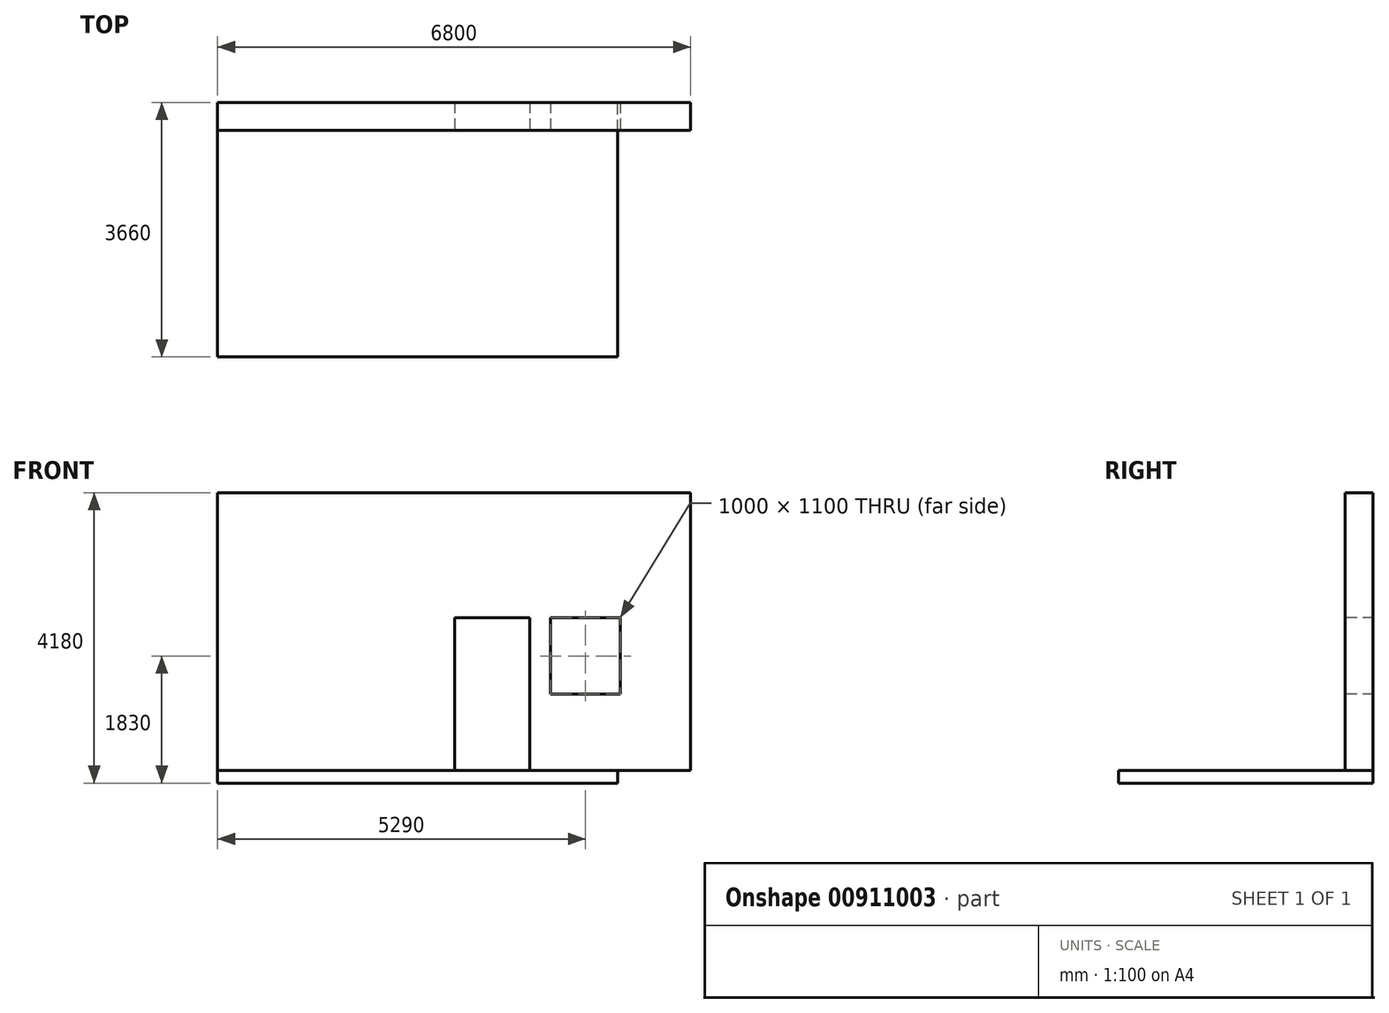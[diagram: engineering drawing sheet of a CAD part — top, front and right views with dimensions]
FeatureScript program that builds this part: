
annotation { "Feature Type Name" : "Feature", "Feature Type Description" : "" }
export const myFeature = defineFeature(function(context is Context, id is Id, definition is map)
    precondition{}
    {
        {
            var Q0;
            Q0=qCreatedBy(makeId("Top.planeOp"),FACE);
            var sketch = newSketch(context, id + "F0", { "sketchPlane" : qUnion([Q0])});
            skLineSegment(sketch, "E0.bottom", {"start": v(0, 0) * mm, "end": v(5750, 0) * mm});
            skLineSegment(sketch, "E0.top", {"start": v(0, 3500) * mm, "end": v(5750, 3500) * mm});
            skLineSegment(sketch, "E0.left", {"start": v(0, 0) * mm, "end": v(0, 3500) * mm});
            skLineSegment(sketch, "E0.right", {"start": v(5750, 0) * mm, "end": v(5750, 3500) * mm});
            skSolve(sketch);
        }
        {
            var Q0;
            Q0=makeQuery(id+"F0.imprint","IMPRINT",FACE,{"disambiguationData":[TD([[makeQuery(id+"F0.imprint","IMPRINT",EDGE,{"derivedFrom":sQuery(id+"F0.wireOp",EDGE,"E0.bottom")}),1.0]])]});
            extrude(context, id + "F1", {"entities" : qUnion([Q0]), "depth" : 180 * mm, "offsetDistance" : 25 * mm});
        }
        {
            var Q0;
            Q0=makeQuery(id+"F1.opExtrude","SWEPT_FACE",FACE,{"disambiguationData":[OSD([sQuery(id+"F0.wireOp",EDGE,"E0.top")])]});
            var sketch = newSketch(context, id + "F2", { "sketchPlane" : qUnion([Q0])});
            skLineSegment(sketch, "E1.bottom", {"start": v(-5750, 180) * mm, "end": v(0, 180) * mm});
            skLineSegment(sketch, "E1.top", {"start": v(-5750, 0) * mm, "end": v(0, 0) * mm});
            skLineSegment(sketch, "E1.left", {"start": v(-5750, 180) * mm, "end": v(-5750, 0) * mm});
            skLineSegment(sketch, "E1.right", {"start": v(0, 180) * mm, "end": v(0, 0) * mm});
            skSolve(sketch);
        }
        {
            var Q0;
            Q0=makeQuery(id+"F2.imprint","IMPRINT",FACE,{"disambiguationData":[TD([[makeQuery(id+"F2.imprint","IMPRINT",EDGE,{"derivedFrom":sQuery(id+"F2.wireOp",EDGE,"E1.bottom")}),1.0]])]});
            extrude(context, id + "F3", {"entities" : qUnion([Q0]), "operationType" : NewBodyOperationType.ADD, "depth" : 160 * mm, "offsetDistance" : 25 * mm});
        }
        {
            var Q0;
            Q0=makeQuery(id+"F3.boolean.opBoolean","MERGE",FACE,{"derivedFrom":[makeQuery(id+"F1.opExtrude","CAP_FACE",FACE,{"disambiguationData":[OSD([sQuery(id+"F0.wireOp",EDGE,"E0.bottom"),sQuery(id+"F0.wireOp",EDGE,"E0.top"),sQuery(id+"F0.wireOp",EDGE,"E0.left"),sQuery(id+"F0.wireOp",EDGE,"E0.right")])],"isStart":false}),makeQuery(id+"F3.opExtrude","SWEPT_FACE",FACE,{"disambiguationData":[OSD([sQuery(id+"F2.wireOp",EDGE,"E1.bottom")])]})]});
            var sketch = newSketch(context, id + "F4", { "sketchPlane" : qUnion([Q0])});
            skLineSegment(sketch, "E2.bottom", {"start": v(0, 3660) * mm, "end": v(6800, 3660) * mm});
            skLineSegment(sketch, "E2.top", {"start": v(0, 3460) * mm, "end": v(6800, 3460) * mm});
            skLineSegment(sketch, "E2.left", {"start": v(0, 3660) * mm, "end": v(0, 3460) * mm});
            skLineSegment(sketch, "E3", {"start": v(6800, 3660) * mm, "end": v(6800, 3460) * mm});
            skSolve(sketch);
        }
        {
            var Q0;
            Q0=makeQuery(id+"F4.imprint","IMPRINT",FACE,{"disambiguationData":[TD([[makeQuery(id+"F4.imprint","IMPRINT",EDGE,{"derivedFrom":sQuery(id+"F4.wireOp",EDGE,"E2.bottom")}),-1.0]])]});
            extrude(context, id + "F5", {"entities" : qUnion([Q0]), "operationType" : NewBodyOperationType.ADD, "depth" : 4000 * mm, "offsetDistance" : 25 * mm});
        }
        {
            var Q0;
            Q0=makeQuery(id+"F5.opExtrude","SWEPT_FACE",FACE,{"disambiguationData":[OSD([sQuery(id+"F4.wireOp",EDGE,"E2.top")])]});
            var sketch = newSketch(context, id + "F6", { "sketchPlane" : qUnion([Q0])});
            skLineSegment(sketch, "E4.bottom", {"start": v(3410, 180) * mm, "end": v(4490, 180) * mm});
            skLineSegment(sketch, "E4.top", {"start": v(3410, 2380) * mm, "end": v(4490, 2380) * mm});
            skLineSegment(sketch, "E4.left", {"start": v(3410, 180) * mm, "end": v(3410, 2380) * mm});
            skLineSegment(sketch, "E4.right", {"start": v(4490, 180) * mm, "end": v(4490, 2380) * mm});
            skLineSegment(sketch, "E5.bottom", {"start": v(4790, 2380) * mm, "end": v(5790, 2380) * mm});
            skLineSegment(sketch, "E5.top", {"start": v(4790, 1280) * mm, "end": v(5790, 1280) * mm});
            skLineSegment(sketch, "E5.left", {"start": v(4790, 2380) * mm, "end": v(4790, 1280) * mm});
            skLineSegment(sketch, "E5.right", {"start": v(5790, 2380) * mm, "end": v(5790, 1280) * mm});
            skSolve(sketch);
        }
        {
            var Q0;
            Q0 = qSketchRegion(id + "F6", true);
            extrude(context, id + "F7", {"entities" : qUnion([Q0]), "operationType" : NewBodyOperationType.REMOVE, "endBound" : BoundingType.THROUGH_ALL, "oppositeDirection" : true, "depth" : 25 * mm, "offsetDistance" : 25 * mm});
        }
        {
            var Q0;
            Q0=makeQuery(id+"F5.opExtrude","SWEPT_FACE",FACE,{"disambiguationData":[OSD([sQuery(id+"F4.wireOp",EDGE,"E2.top")])]});
            extrude(context, id + "F8", {"entities" : qUnion([Q0]), "operationType" : NewBodyOperationType.ADD, "depth" : 200 * mm, "offsetDistance" : 25 * mm});
        }
    });
